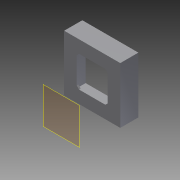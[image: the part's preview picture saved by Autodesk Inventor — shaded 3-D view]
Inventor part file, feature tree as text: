
AUTODESK INVENTOR PART (.ipt)
format: ipt  version: 2012 (Build 160160000, 160)  size: 59,392 bytes
history: native  units: in
note: dims shown in document units (in); Inventor stores cm internally (conversion verified against a paired STEP export)
features: plane x1
ambient origin geometry x8: Origin, YZ Plane, XZ Plane, XY Plane, X Axis, Y Axis, Z Axis, Center Point
feature tree (1):
  plane  "Work Plane2"
